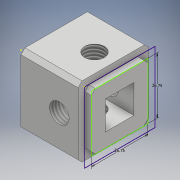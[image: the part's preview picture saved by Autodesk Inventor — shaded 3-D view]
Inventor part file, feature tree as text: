
AUTODESK INVENTOR PART (.ipt)
format: ipt  version: 2017 (Build 210142000, 142)  size: 162,816 bytes
history: native  units: mm
features: sketch x8, extrude x5, thread x4, chamfer x1
ambient origin geometry x8: Origin, YZ Plane, XZ Plane, XY Plane, X Axis, Y Axis, Z Axis, Center Point
bodies: Solid1 (feature_tree)
feature tree (18):
  extrude  "Extrusion1"  Depth=33.25mm
  sketch  "Sketch2"  dims[d2=30.0mm d3=0.0mm d4=26.75mm]
  sketch  "Sketch3"  dims[d5=26.75mm]
  extrude  "Extrusion2"  Depth=26.75mm
  chamfer  "Chamfer1"  Distance=3.0mm
  extrude  "Extrusion3"  Depth=13.5mm
  sketch  "Sketch6"  dims[d10=1.875mm d11=2.0mm d12=45.0deg d13=13.5mm]
  extrude  "Extrusion4"  Depth=6.625mm
  extrude  "Extrusion5"  Depth=26.75mm TaperAngle=0.0deg
  thread  "Thread1"  [1 undecoded]
  thread  "Thread2"  [1 undecoded]
  thread  "Thread3"  [1 undecoded]
  thread  "Thread4"  [1 undecoded]
  sketch  "Sketch1"  dims[d0=33.25mm d1=33.25mm]
  sketch  "Sketch4"  dims[d6=26.75mm]
  sketch  "Sketch5"  dims[d7=26.75mm d8=3.0mm d9=0.0mm]
  sketch  "Sketch7"  dims[d14=13.5mm d15=6.625mm]
  sketch  "Sketch8"  dims[d16=6.625mm d17=26.75mm d18=0.0mm d19=9.25mm d20=33.25mm d21=0.0mm d22=9.25mm d23=33.25mm d24=0.0mm d25=10.0mm d26=0.0mm d27=10.0mm d28=0.0mm d29=10.0mm d30=0.0mm d31=10.0mm d32=0.0mm]
note: 4 required parameter values undecoded (feature->parameter linkage not recoverable at this tier; creation-order binding heuristic only, values carry confidence <= 0.55)
